# Revit family: Athletic-Team-Bench
name_source: partatom
category: Generic Models
units: mm (PartAtom-declared; Revit-internal decimal feet)

## family parameters
Always vertical = Yes
Can host rebar = No
Classification Number = 23.40.20.14.14.21
Cut with Voids When Loaded = No
Maintain Annotation Orientation = No
Part Type = Normal
Room Calculation Point = No
Round Connector Dimension = Use Diameter
Shared = No
Work Plane-Based = No

## types (1)
- Athletic-Team-Bench
    Assembly Code = E1020900
    Bench Length = 6' - 0"
    Bench Material = ARCAT - Metal - Aluminum_Anodized_Blue
    Bench Width = 0' - 10"
    Construction Details = http://www.arcat.com
    Default Elevation = 0' - 0"
    Description = Outdoor Athletic Team Bench
    Expected Lifespan (Years) = 0
    Green Building - LEED = http://www.arcat.com
    Height = 1' - 4"
    Keynote = 10500
    Leg Material = ARCAT - Metal - Aluminum_Anodized_Clear
    Maintenance Schedule (Months) = 0
    Manufacturer = Generic
    Manufacturer Fax = (203) 929-9444
    Manufacturer Website = http://www.arcat.com
    Model = Generic
    Product Data = http://www.arcat.com
    Product Properties = http://www.arcat.com
    Seating Capacity = 5
    Specification = http://www.arcat.com
    Warranty Duration (Years) = 0
    Weight Capacity = 1500.00 lb

## geometry (parser evidence)
native form markers: Sweep x2
no freeform markers — native parametric forms only
